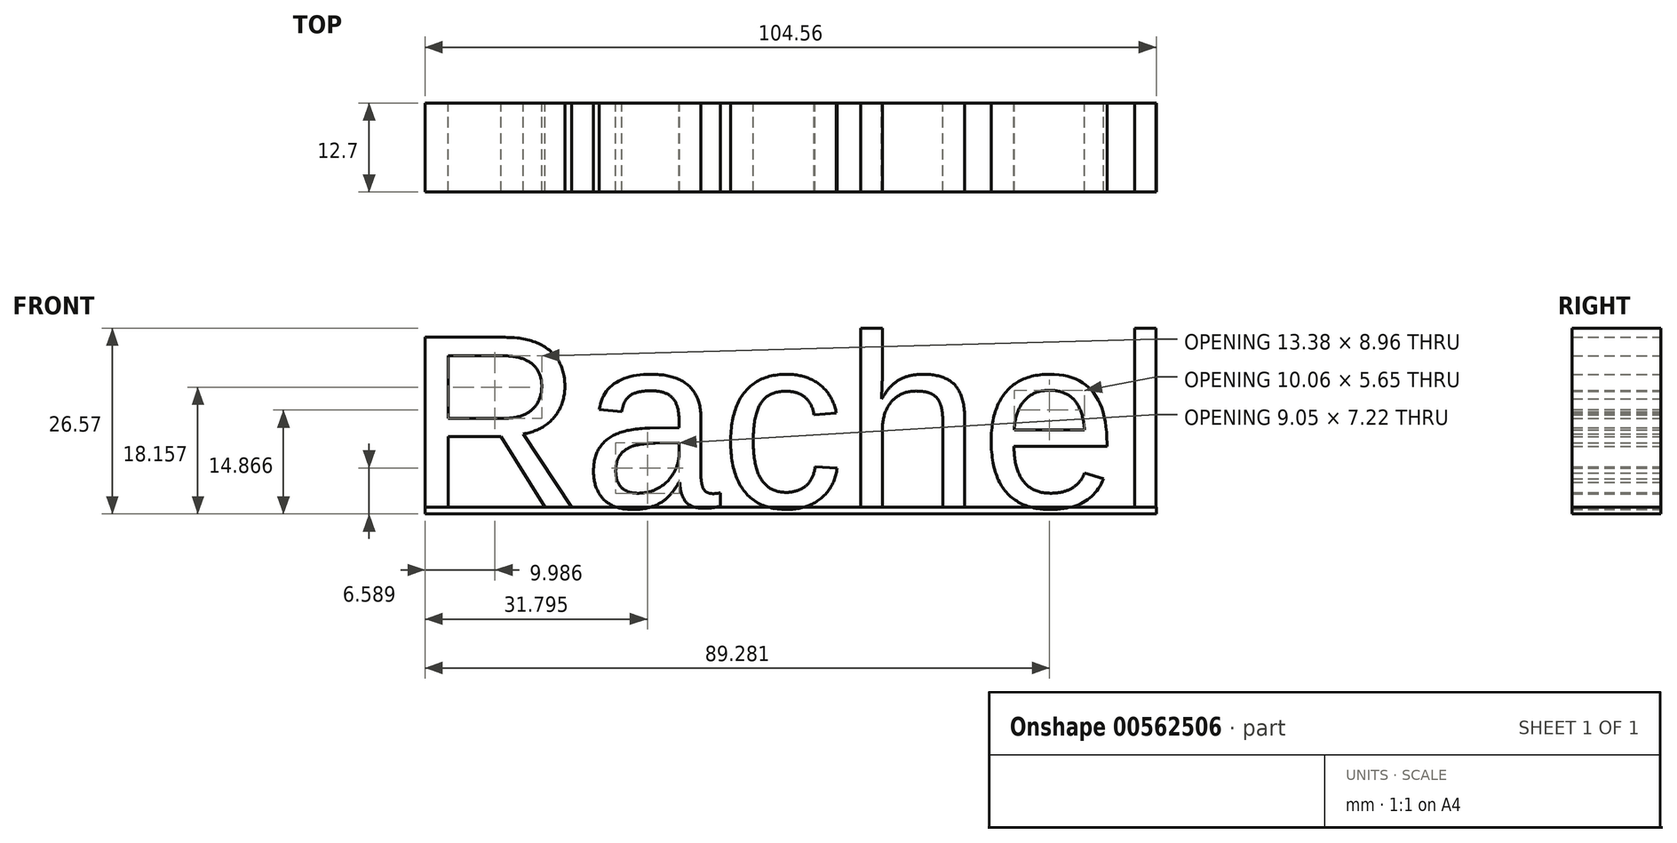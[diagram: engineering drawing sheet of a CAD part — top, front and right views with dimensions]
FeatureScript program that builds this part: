
annotation { "Feature Type Name" : "Feature", "Feature Type Description" : "" }
export const myFeature = defineFeature(function(context is Context, id is Id, definition is map)
    precondition{}
    {
        {
            var Q0;
            Q0=qCreatedBy(makeId("Front.planeOp"),FACE);
            var sketch = newSketch(context, id + "F0", { "sketchPlane" : qUnion([Q0])});
            skText(sketch, "E0", { "text": "Rachel", "fontName": "Arimo-Regular.ttf"});
            skPoint(sketch, "E1", {"position": v(0, 12.7) * mm});
            const initialGuessF0  = {"E0": [-0.05495, 0, 1, 0, 0.0254]};
            skSetInitialGuess(sketch, initialGuessF0);
            skSolve(sketch);
        }
        {
            var Q0;
            Q0=qSketchRegion(id+"F0",true);
            extrude(context, id + "F1", {"entities" : qUnion([Q0]), "endBound" : BoundingType.SYMMETRIC, "depth" : 12.7 * mm, "offsetDistance" : 25.4 * mm});
        }
        {
            var Q0;
            Q0=qCreatedBy(makeId("Top.planeOp"),FACE);
            var sketch = newSketch(context, id + "F2", { "sketchPlane" : qUnion([Q0])});
            skLineSegment(sketch, "E2.0", {"start": v(52.5, -6.35) * mm, "end": v(52.5, 6.35) * mm});
            skLineSegment(sketch, "E3.0", {"start": v(-52.05, -6.35) * mm, "end": v(-52.05, 6.35) * mm});
            skLineSegment(sketch, "E4", {"start": v(-52.05, -6.35) * mm, "end": v(52.5, -6.35) * mm});
            skLineSegment(sketch, "E5", {"start": v(52.5, 6.35) * mm, "end": v(-52.05, 6.35) * mm});
            skSolve(sketch);
        }
        {
            var Q0;
            Q0=makeQuery(id+"F2.imprint","IMPRINT",FACE,{"disambiguationData":[TD([[makeQuery(id+"F2.imprint","IMPRINT",EDGE,{"derivedFrom":sQuery(id+"F2.wireOp",EDGE,"E2.0")}),1.0]])]});
            extrude(context, id + "F3", {"entities" : qUnion([Q0]), "oppositeDirection" : true, "depth" : 1 * mm, "offsetDistance" : 25.4 * mm});
        }
    });
